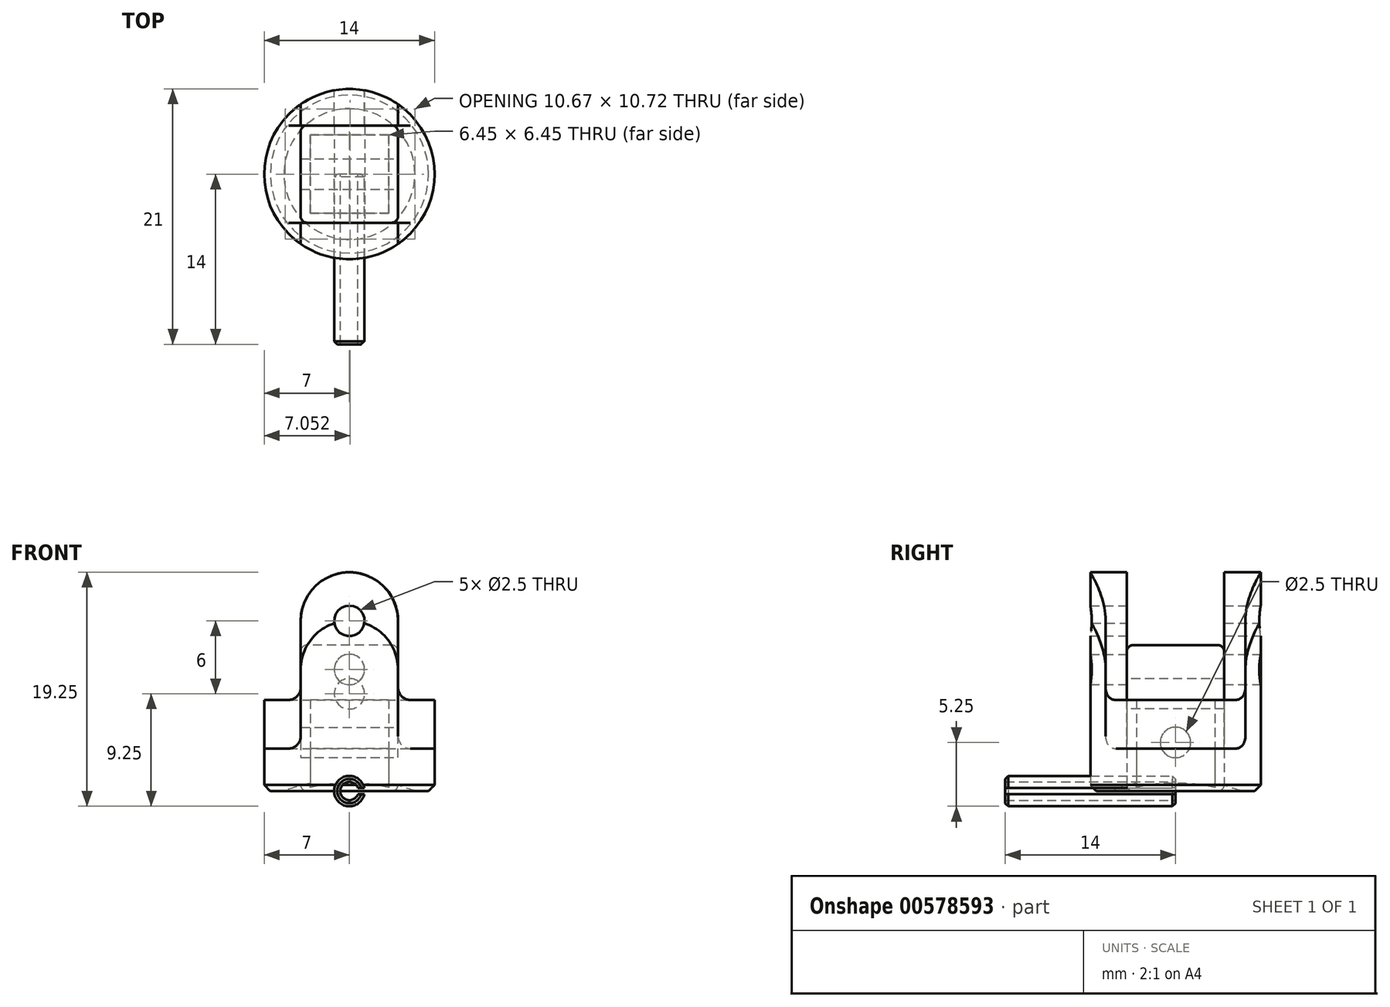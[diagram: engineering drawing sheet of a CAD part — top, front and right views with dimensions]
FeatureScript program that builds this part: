
annotation { "Feature Type Name" : "Feature", "Feature Type Description" : "" }
export const myFeature = defineFeature(function(context is Context, id is Id, definition is map)
    precondition{}
    {
        {
            var Q0;
            Q0=qCreatedBy(makeId("Top.planeOp"),FACE);
            var sketch = newSketch(context, id + "F0", { "sketchPlane" : qUnion([Q0])});
            skLineSegment(sketch, "E0.bottom", {"start": v(3.17, -3.17) * mm, "end": v(-3.17, -3.18) * mm});
            skLineSegment(sketch, "E0.top", {"start": v(3.17, 3.18) * mm, "end": v(-3.17, 3.17) * mm});
            skLineSegment(sketch, "E0.left", {"start": v(3.17, -3.17) * mm, "end": v(3.17, 3.17) * mm});
            skLineSegment(sketch, "E0.right", {"start": v(-3.17, -3.18) * mm, "end": v(-3.17, 3.17) * mm});
            skPoint(sketch, "E0.middle", {"position": v(0, 0) * mm});
            skCircle(sketch, "E1", {"center": v(0, 0) * mm, "radius": 7 * mm});
            skSolve(sketch);
        }
        {
            var Q0;
            Q0=qCreatedBy(makeId("Front.planeOp"),FACE);
            var sketch = newSketch(context, id + "F1", { "sketchPlane" : qUnion([Q0])});
            skLineSegment(sketch, "E2", {"start": v(-7, 0) * mm, "end": v(-7, 3.5) * mm});
            skLineSegment(sketch, "E3", {"start": v(-7, 3.5) * mm, "end": v(-5, 3.5) * mm});
            skLineSegment(sketch, "E4", {"start": v(-4, 4.5) * mm, "end": v(-4, 10) * mm});
            skLineSegment(sketch, "E5", {"start": v(0, 14) * mm, "end": v(0, 14) * mm});
            skLineSegment(sketch, "E6", {"start": v(4, 10) * mm, "end": v(4, 4.5) * mm});
            skLineSegment(sketch, "E7", {"start": v(5, 3.5) * mm, "end": v(7, 3.5) * mm});
            skLineSegment(sketch, "E8", {"start": v(7, 3.5) * mm, "end": v(7, 0) * mm});
            skLineSegment(sketch, "E9", {"start": v(7, 0) * mm, "end": v(-7, 0) * mm});
            skCircle(sketch, "E10", {"center": v(0, 10) * mm, "radius": 1.25 * mm});
            skPoint(sketch, "E11.visualSharp", {"position": v(-4, 3.5) * mm});
            skArc(sketch, "E11.filletArc", {"start": v(-5, 3.5) * mm, "mid": v(-4.3, 3.8) * mm, "end": v(-4, 4.5) * mm});
            skPoint(sketch, "E12.visualSharp", {"position": v(4, 3.5) * mm});
            skArc(sketch, "E12.filletArc", {"start": v(4, 4.5) * mm, "mid": v(4.3, 3.8) * mm, "end": v(5, 3.5) * mm});
            skPoint(sketch, "E13.visualSharp", {"position": v(-4, 14) * mm});
            skArc(sketch, "E13.filletArc", {"start": v(0, 14) * mm, "mid": v(-2.83, 12.83) * mm, "end": v(-4, 10) * mm});
            skPoint(sketch, "E14.visualSharp", {"position": v(4, 14) * mm});
            skArc(sketch, "E14.filletArc", {"start": v(4, 10) * mm, "mid": v(2.83, 12.83) * mm, "end": v(0, 14) * mm});
            skSolve(sketch);
        }
        {
            var Q0;
            Q0=qCreatedBy(makeId("Right.planeOp"),FACE);
            var sketch = newSketch(context, id + "F2", { "sketchPlane" : qUnion([Q0])});
            skLineSegment(sketch, "E15.bottom", {"start": v(4, 3.5) * mm, "end": v(-4, 3.5) * mm});
            skLineSegment(sketch, "E15.top", {"start": v(4, 14) * mm, "end": v(-4, 14) * mm});
            skLineSegment(sketch, "E15.left", {"start": v(4, 3.5) * mm, "end": v(4, 14) * mm});
            skLineSegment(sketch, "E15.right", {"start": v(-4, 3.5) * mm, "end": v(-4, 14) * mm});
            skPoint(sketch, "E15.middle", {"position": v(0, 8.75) * mm});
            skSolve(sketch);
        }
        {
            var Q0;
            Q0=makeQuery(id+"F0.imprint","IMPRINT",FACE,{"disambiguationData":[TD([[makeQuery(id+"F0.imprint","IMPRINT",EDGE,{"derivedFrom":sQuery(id+"F0.wireOp",EDGE,"E0.bottom")}),1.0]])]});
            var Q1;
            Q1=makeQuery(id+"F0.imprint","IMPRINT",FACE,{"disambiguationData":[TD([[makeQuery(id+"F0.imprint","IMPRINT",EDGE,{"derivedFrom":sQuery(id+"F0.wireOp",EDGE,"E0.bottom")}),-1.0]])]});
            extrude(context, id + "F3", {"entities" : qUnion([Q0, Q1]), "depth" : 14 * mm, "offsetDistance" : 25 * mm});
        }
        {
            var Q0;
            Q0 = qSketchRegion(id + "F1", true);
            extrude(context, id + "F4", {"entities" : qUnion([Q0]), "operationType" : NewBodyOperationType.INTERSECT, "endBound" : BoundingType.THROUGH_ALL, "depth" : 25 * mm, "offsetDistance" : 25 * mm, "hasSecondDirection" : true, "secondDirectionBound" : SecondDirectionBoundingType.THROUGH_ALL, "secondDirectionOppositeDirection" : true, "secondDirectionDepth" : 25 * mm});
        }
        {
            var Q0;
            Q0 = qSketchRegion(id + "F2", true);
            extrude(context, id + "F5", {"entities" : qUnion([Q0]), "operationType" : NewBodyOperationType.REMOVE, "endBound" : BoundingType.THROUGH_ALL, "oppositeDirection" : true, "depth" : 25 * mm, "offsetDistance" : 25 * mm, "hasSecondDirection" : true, "secondDirectionBound" : SecondDirectionBoundingType.THROUGH_ALL, "secondDirectionOppositeDirection" : false, "secondDirectionDepth" : 25 * mm});
        }
        {
            var Q0;
            Q0=makeQuery(id+"F3.opExtrude","SWEPT_BODY",BODY,{"disambiguationData":[OSD([sQuery(id+"F0.wireOp",EDGE,"E1")])]});
            transform(context, id + "F6", {"entities" : qUnion([Q0]), "transformType" : TransformType.TRANSLATION_3D, "dx" : 0 * mm, "dy" : 0 * mm, "dz" : 0 * mm, "makeCopy" : true});
        }
        {
            var Q0;
            Q0=makeQuery(id+"F6.opPattern","COPY",BODY,{"derivedFrom":makeQuery(id+"F3.opExtrude","SWEPT_BODY",BODY,{"disambiguationData":[OSD([sQuery(id+"F0.wireOp",EDGE,"E1")])]}),"instanceName":"1"});
            deleteBodies(context, id + "F7", {"entities" : qUnion([Q0])});
        }
        {
            var Q0;
            Q0=makeQuery(id+"F0.imprint","IMPRINT",FACE,{"disambiguationData":[TD([[makeQuery(id+"F0.imprint","IMPRINT",EDGE,{"derivedFrom":sQuery(id+"F0.wireOp",EDGE,"E0.bottom")}),-1.0]])]});
            extrude(context, id + "F8", {"entities" : qUnion([Q0]), "operationType" : NewBodyOperationType.ADD, "oppositeDirection" : true, "depth" : 8.5 * mm, "offsetDistance" : 25 * mm});
        }
        {
            var Q0;
            Q0=makeQuery(id+"F8.opExtrude","CAP_FACE",FACE,{"disambiguationData":[OSD([sQuery(id+"F0.wireOp",EDGE,"E0.bottom"),sQuery(id+"F0.wireOp",EDGE,"E0.top"),sQuery(id+"F0.wireOp",EDGE,"E0.left"),sQuery(id+"F0.wireOp",EDGE,"E0.right")])],"isStart":false});
            var Q1;
            Q1=makeQuery(id+"F8.opExtrude","SWEPT_EDGE",EDGE,{"disambiguationData":[OSD([sQuery(id+"F0.wireOp",EDGE,"E0.bottom"),sQuery(id+"F0.wireOp",EDGE,"E0.right")])]});
            var Q2;
            Q2=makeQuery(id+"F8.opExtrude","SWEPT_EDGE",EDGE,{"disambiguationData":[OSD([sQuery(id+"F0.wireOp",EDGE,"E0.bottom"),sQuery(id+"F0.wireOp",EDGE,"E0.left")])]});
            var Q3;
            Q3=makeQuery(id+"F8.opExtrude","SWEPT_EDGE",EDGE,{"disambiguationData":[OSD([sQuery(id+"F0.wireOp",EDGE,"E0.top"),sQuery(id+"F0.wireOp",EDGE,"E0.right")])]});
            var Q4;
            Q4=makeQuery(id+"F8.opExtrude","SWEPT_EDGE",EDGE,{"disambiguationData":[OSD([sQuery(id+"F0.wireOp",EDGE,"E0.top"),sQuery(id+"F0.wireOp",EDGE,"E0.left")])]});
            var Q5;
            Q5=makeQuery(id+"F3.opExtrude","CAP_EDGE",EDGE,{"disambiguationData":[OSD([sQuery(id+"F0.wireOp",EDGE,"E1")])],"isStart":true});
            chamfer(context, id + "F9", {"entities" : qUnion([Q0, Q1, Q2, Q3, Q4, Q5]), "width" : 0.5 * mm, "tangentPropagation" : true});
        }
        {
            var Q0;
            Q0=makeQuery(id+"F8.opExtrude","SWEPT_FACE",FACE,{"disambiguationData":[OSD([sQuery(id+"F0.wireOp",EDGE,"E0.bottom")])]});
            var sketch = newSketch(context, id + "F10", { "sketchPlane" : qUnion([Q0])});
            skPoint(sketch, "E16", {"position": v(0, -5) * mm});
            skSolve(sketch);
        }
        {
            var Q0;
            Q0=sQuery(id+"F10.wireOp",VERTEX,"E16");
            var Q1;
            Q1=makeQuery(id+"F3.opExtrude","SWEPT_BODY",BODY,{"disambiguationData":[OSD([sQuery(id+"F0.wireOp",EDGE,"E1")])]});
            hole(context, id + "F11", {"style" : HoleStyle.SIMPLE, "endStyle" : HoleEndStyle.BLIND, "holeDiameter" : 2.5 * mm, "holeDepth" : 4 * mm, "tappedDepth" : 20 * mm, "tapClearance" : 0, "startFromSketch" : true, "locations" : qUnion([Q0]), "scope" : qUnion([Q1])});
        }
        {
            var Q0;
            Q0=qCreatedBy(makeId("Front.planeOp"),FACE);
            var sketch = newSketch(context, id + "F12", { "sketchPlane" : qUnion([Q0])});
            skLineSegment(sketch, "E17", {"start": v(-7, 0) * mm, "end": v(-7, 7.5) * mm});
            skLineSegment(sketch, "E18", {"start": v(-7, 7.5) * mm, "end": v(-5, 7.5) * mm});
            skLineSegment(sketch, "E19", {"start": v(-4, 8.5) * mm, "end": v(-4, 14) * mm});
            skLineSegment(sketch, "E20", {"start": v(0, 18) * mm, "end": v(0, 18) * mm});
            skLineSegment(sketch, "E21", {"start": v(4, 14) * mm, "end": v(4, 8.5) * mm});
            skLineSegment(sketch, "E22", {"start": v(5, 7.5) * mm, "end": v(7, 7.5) * mm});
            skLineSegment(sketch, "E23", {"start": v(7, 7.5) * mm, "end": v(7, 0) * mm});
            skLineSegment(sketch, "E24", {"start": v(7, 0) * mm, "end": v(-7, 0) * mm});
            skPoint(sketch, "E25.visualSharp", {"position": v(-4, 7.5) * mm});
            skArc(sketch, "E25.filletArc", {"start": v(-5, 7.5) * mm, "mid": v(-4.3, 7.8) * mm, "end": v(-4, 8.5) * mm});
            skPoint(sketch, "E26.visualSharp", {"position": v(4, 7.5) * mm});
            skArc(sketch, "E26.filletArc", {"start": v(4, 8.5) * mm, "mid": v(4.3, 7.8) * mm, "end": v(5, 7.5) * mm});
            skPoint(sketch, "E27.visualSharp", {"position": v(-4, 18) * mm});
            skArc(sketch, "E27.filletArc", {"start": v(0, 18) * mm, "mid": v(-2.83, 16.83) * mm, "end": v(-4, 14) * mm});
            skPoint(sketch, "E28.visualSharp", {"position": v(4, 18) * mm});
            skArc(sketch, "E28.filletArc", {"start": v(4, 14) * mm, "mid": v(2.83, 16.83) * mm, "end": v(0, 18) * mm});
            skCircle(sketch, "E29", {"center": v(0, 14) * mm, "radius": 1.25 * mm});
            skSolve(sketch);
        }
        {
            var Q0;
            Q0=makeQuery(id+"F0.imprint","IMPRINT",FACE,{"disambiguationData":[TD([[makeQuery(id+"F0.imprint","IMPRINT",EDGE,{"derivedFrom":sQuery(id+"F0.wireOp",EDGE,"E0.bottom")}),1.0]])]});
            var Q1;
            Q1=makeQuery(id+"F0.imprint","IMPRINT",FACE,{"disambiguationData":[TD([[makeQuery(id+"F0.imprint","IMPRINT",EDGE,{"derivedFrom":sQuery(id+"F0.wireOp",EDGE,"E0.bottom")}),-1.0]])]});
            extrude(context, id + "F13", {"entities" : qUnion([Q0, Q1]), "depth" : 18 * mm, "offsetDistance" : 25 * mm});
        }
        {
            var Q0;
            Q0 = qSketchRegion(id + "F12", true);
            extrude(context, id + "F14", {"entities" : qUnion([Q0]), "operationType" : NewBodyOperationType.INTERSECT, "endBound" : BoundingType.THROUGH_ALL, "depth" : 25 * mm, "offsetDistance" : 25 * mm, "hasSecondDirection" : true, "secondDirectionBound" : SecondDirectionBoundingType.THROUGH_ALL, "secondDirectionOppositeDirection" : true, "secondDirectionDepth" : 25 * mm});
        }
        {
            var Q0;
            Q0=qCreatedBy(makeId("Right.planeOp"),FACE);
            var sketch = newSketch(context, id + "F15", { "sketchPlane" : qUnion([Q0])});
            skLineSegment(sketch, "E30.bottom", {"start": v(4, 7.5) * mm, "end": v(-4, 7.5) * mm});
            skLineSegment(sketch, "E30.top", {"start": v(4, 18) * mm, "end": v(-4, 18) * mm});
            skLineSegment(sketch, "E30.left", {"start": v(4, 7.5) * mm, "end": v(4, 18) * mm});
            skLineSegment(sketch, "E30.right", {"start": v(-4, 7.5) * mm, "end": v(-4, 18) * mm});
            skPoint(sketch, "E30.middle", {"position": v(0, 12.75) * mm});
            skSolve(sketch);
        }
        {
            var Q0;
            Q0 = qSketchRegion(id + "F15", true);
            extrude(context, id + "F16", {"entities" : qUnion([Q0]), "operationType" : NewBodyOperationType.REMOVE, "endBound" : BoundingType.THROUGH_ALL, "oppositeDirection" : true, "depth" : 25 * mm, "offsetDistance" : 25 * mm, "hasSecondDirection" : true, "secondDirectionBound" : SecondDirectionBoundingType.THROUGH_ALL, "secondDirectionOppositeDirection" : false, "secondDirectionDepth" : 25 * mm});
        }
        {
            var Q0;
            Q0=makeQuery(id+"F0.imprint","IMPRINT",FACE,{"disambiguationData":[TD([[makeQuery(id+"F0.imprint","IMPRINT",EDGE,{"derivedFrom":sQuery(id+"F0.wireOp",EDGE,"E0.bottom")}),1.0]])]});
            var sketch = newSketch(context, id + "F17", { "sketchPlane" : qUnion([Q0])});
            skLineSegment(sketch, "E31.0", {"start": v(3.23, -3.23) * mm, "end": v(3.23, 3.23) * mm});
            skLineSegment(sketch, "E31.1", {"start": v(-3.23, -3.23) * mm, "end": v(3.22, -3.23) * mm});
            skLineSegment(sketch, "E31.2", {"start": v(-3.23, 3.23) * mm, "end": v(-3.23, -3.23) * mm});
            skLineSegment(sketch, "E31.3", {"start": v(3.23, 3.23) * mm, "end": v(-3.22, 3.23) * mm});
            skSolve(sketch);
        }
        {
            var Q0;
            Q0 = qSketchRegion(id + "F17", true);
            extrude(context, id + "F18", {"entities" : qUnion([Q0]), "operationType" : NewBodyOperationType.REMOVE, "endBound" : BoundingType.THROUGH_ALL, "depth" : 25 * mm, "offsetDistance" : 25 * mm});
        }
        {
            var Q0;
            Q0=makeQuery(id+"F13.opExtrude","CAP_EDGE",EDGE,{"disambiguationData":[OSD([sQuery(id+"F0.wireOp",EDGE,"E1")])],"isStart":true});
            chamfer(context, id + "F19", {"entities" : qUnion([Q0]), "width" : 0.5 * mm, "tangentPropagation" : true});
        }
        {
            var Q0;
            Q0=sQuery(id+"F0.wireOp",VERTEX,"E0.right.start");
            var Q1;
            Q1=sQuery(id+"F0.wireOp",VERTEX,"E0.left.end");
            var Q2;
            Q2=sQuery(id+"F12.wireOp",VERTEX,"E29.center");
            cPlane(context, id + "F20", {"entities" : qUnion([Q0, Q1, Q2]), "cplaneType" : CPlaneType.THREE_POINT, "offset" : 25 * mm, "width" : 150 * mm, "height" : 150 * mm});
        }
        {
            var Q0;
            Q0=qCreatedBy(id+"F20.planeOp",FACE);
            var sketch = newSketch(context, id + "F21", { "sketchPlane" : qUnion([Q0])});
            skLineSegment(sketch, "E32", {"start": v(0, -29) * mm, "end": v(0, 1) * mm});
            skArc(sketch, "E33", {"start": v(0, 1) * mm, "mid": v(-15, -14.06) * mm, "end": v(0.12, -29) * mm});
            skSolve(sketch);
        }
        {
            var Q0;
            {var subQ0=sQuery(id+"F21.wireOp",EDGE,"E32");Q0=makeQuery(id+"F21.imprint","IMPRINT",FACE,{"disambiguationData":[TD([[makeQuery(id+"F21.imprint","IMPRINT",EDGE,{"derivedFrom":subQ0}),1.0]])]});}
            var Q1;
            Q1=sQuery(id+"F21.wireOp",EDGE,"E32");
            revolve(context, id + "F22", {"operationType" : NewBodyOperationType.REMOVE, "entities" : qUnion([Q0]), "axis" : qUnion([Q1]), "revolveType" : RevolveType.FULL, "oppositeDirection" : true});
        }
        {
            var Q0;
            Q0=qCreatedBy(makeId("Top.planeOp"),FACE);
            var sketch = newSketch(context, id + "F23", { "sketchPlane" : qUnion([Q0])});
            skLineSegment(sketch, "E34.bottom", {"start": v(3.5, -4) * mm, "end": v(-3.5, -4) * mm});
            skLineSegment(sketch, "E34.top", {"start": v(3.5, 4) * mm, "end": v(-3.5, 4) * mm});
            skLineSegment(sketch, "E34.left", {"start": v(4, -3.5) * mm, "end": v(4, 3.5) * mm});
            skLineSegment(sketch, "E34.right", {"start": v(-4, -3.5) * mm, "end": v(-4, 3.5) * mm});
            skPoint(sketch, "E34.middle", {"position": v(0, 0) * mm});
            skPoint(sketch, "E35.visualSharp", {"position": v(-4, 4) * mm});
            skArc(sketch, "E35.filletArc", {"start": v(-3.5, 4) * mm, "mid": v(-3.85, 3.85) * mm, "end": v(-4, 3.5) * mm});
            skPoint(sketch, "E36.visualSharp", {"position": v(4, 4) * mm});
            skArc(sketch, "E36.filletArc", {"start": v(4, 3.5) * mm, "mid": v(3.85, 3.85) * mm, "end": v(3.5, 4) * mm});
            skPoint(sketch, "E37.visualSharp", {"position": v(-4, -4) * mm});
            skArc(sketch, "E37.filletArc", {"start": v(-4, -3.5) * mm, "mid": v(-3.85, -3.85) * mm, "end": v(-3.5, -4) * mm});
            skPoint(sketch, "E38.visualSharp", {"position": v(4, -4) * mm});
            skArc(sketch, "E38.filletArc", {"start": v(3.5, -4) * mm, "mid": v(3.85, -3.85) * mm, "end": v(4, -3.5) * mm});
            skSolve(sketch);
        }
        {
            var Q0;
            Q0 = qSketchRegion(id + "F23", true);
            extrude(context, id + "F24", {"entities" : qUnion([Q0]), "depth" : 12 * mm, "offsetDistance" : 25 * mm});
        }
        {
            var Q0;
            Q0=makeQuery(id+"F24.opExtrude","CAP_EDGE",EDGE,{"disambiguationData":[OSD([sQuery(id+"F23.wireOp",EDGE,"E34.bottom")])],"isStart":false});
            var Q1;
            Q1=makeQuery(id+"F24.opExtrude","CAP_EDGE",EDGE,{"disambiguationData":[OSD([sQuery(id+"F23.wireOp",EDGE,"E34.bottom")])],"isStart":true});
            fillet(context, id + "F25", {"entities" : qUnion([Q0, Q1]), "radius" : 0.5 * mm, "tangentPropagation" : true, "allowEdgeOverflow" : false});
        }
        {
            var Q0;
            Q0=makeQuery(id+"F24.opExtrude","SWEPT_FACE",FACE,{"disambiguationData":[OSD([sQuery(id+"F23.wireOp",EDGE,"E34.bottom")])]});
            var sketch = newSketch(context, id + "F26", { "sketchPlane" : qUnion([Q0])});
            skPoint(sketch, "E39", {"position": v(0, 8) * mm});
            skSolve(sketch);
        }
        {
            var Q0;
            Q0=makeQuery(id+"F24.opExtrude","SWEPT_FACE",FACE,{"disambiguationData":[OSD([sQuery(id+"F23.wireOp",EDGE,"E34.left")])]});
            var sketch = newSketch(context, id + "F27", { "sketchPlane" : qUnion([Q0])});
            skPoint(sketch, "E40", {"position": v(0, 4) * mm});
            skSolve(sketch);
        }
        {
            var Q0;
            Q0=sQuery(id+"F27.wireOp",VERTEX,"E40");
            var Q1;
            Q1=makeQuery(id+"F24.opExtrude","SWEPT_BODY",BODY,{"disambiguationData":[OSD([sQuery(id+"F23.wireOp",EDGE,"E34.bottom"),sQuery(id+"F23.wireOp",EDGE,"E34.top"),sQuery(id+"F23.wireOp",EDGE,"E34.left"),sQuery(id+"F23.wireOp",EDGE,"E34.right"),sQuery(id+"F23.wireOp",EDGE,"E35.filletArc"),sQuery(id+"F23.wireOp",EDGE,"E36.filletArc"),sQuery(id+"F23.wireOp",EDGE,"E37.filletArc"),sQuery(id+"F23.wireOp",EDGE,"E38.filletArc")])]});
            hole(context, id + "F28", {"style" : HoleStyle.SIMPLE, "endStyle" : HoleEndStyle.THROUGH, "holeDiameter" : 2.5 * mm, "tappedDepth" : 20 * mm, "tapClearance" : 0, "startFromSketch" : true, "locations" : qUnion([Q0]), "scope" : qUnion([Q1])});
        }
        {
            var Q0;
            Q0=sQuery(id+"F26.wireOp",VERTEX,"E39");
            var Q1;
            Q1=makeQuery(id+"F24.opExtrude","SWEPT_BODY",BODY,{"disambiguationData":[OSD([sQuery(id+"F23.wireOp",EDGE,"E34.bottom"),sQuery(id+"F23.wireOp",EDGE,"E34.top"),sQuery(id+"F23.wireOp",EDGE,"E34.left"),sQuery(id+"F23.wireOp",EDGE,"E34.right"),sQuery(id+"F23.wireOp",EDGE,"E35.filletArc"),sQuery(id+"F23.wireOp",EDGE,"E36.filletArc"),sQuery(id+"F23.wireOp",EDGE,"E37.filletArc"),sQuery(id+"F23.wireOp",EDGE,"E38.filletArc")])]});
            hole(context, id + "F29", {"style" : HoleStyle.SIMPLE, "endStyle" : HoleEndStyle.THROUGH, "holeDiameter" : 2.5 * mm, "tappedDepth" : 20 * mm, "tapClearance" : 0, "startFromSketch" : true, "locations" : qUnion([Q0]), "scope" : qUnion([Q1])});
        }
        {
            var Q0;
            Q0=qCreatedBy(makeId("Front.planeOp"),FACE);
            var sketch = newSketch(context, id + "F30", { "sketchPlane" : qUnion([Q0])});
            skArc(sketch, "E41", {"start": v(1.22, 0.25) * mm, "mid": v(-1.25, 0) * mm, "end": v(1.22, -0.25) * mm});
            skArc(sketch, "E42", {"start": v(0.7, 0.25) * mm, "mid": v(-0.75, 0) * mm, "end": v(0.7, -0.25) * mm});
            skLineSegment(sketch, "E43", {"start": v(0.7, 0.25) * mm, "end": v(1.22, 0.25) * mm});
            skLineSegment(sketch, "E44", {"start": v(0.7, -0.25) * mm, "end": v(1.22, -0.25) * mm});
            skSolve(sketch);
        }
        {
            var Q0;
            Q0=makeQuery(id+"F30.imprint","IMPRINT",FACE,{"disambiguationData":[TD([[makeQuery(id+"F30.imprint","IMPRINT",EDGE,{"derivedFrom":sQuery(id+"F30.wireOp",EDGE,"E41")}),1.0]])]});
            extrude(context, id + "F31", {"entities" : qUnion([Q0]), "depth" : 14 * mm, "offsetDistance" : 25 * mm});
        }
        {
            var Q0;
            Q0=makeQuery(id+"F31.opExtrude","CAP_EDGE",EDGE,{"disambiguationData":[OSD([sQuery(id+"F30.wireOp",EDGE,"E41")])],"isStart":false});
            var Q1;
            Q1=makeQuery(id+"F31.opExtrude","CAP_EDGE",EDGE,{"disambiguationData":[OSD([sQuery(id+"F30.wireOp",EDGE,"E41")])],"isStart":true});
            chamfer(context, id + "F32", {"entities" : qUnion([Q0, Q1]), "width" : 0.25 * mm, "tangentPropagation" : true});
        }
        {
            var Q0;
            Q0=sQuery(id+"F1.wireOp",EDGE,"E10");
            var Q1;
            Q1=makeQuery(id+"F5.boolean.opBoolean","COPY",FACE,{"derivedFrom":makeQuery(id+"F5.opExtrude","SWEPT_FACE",FACE,{"disambiguationData":[OSD([sQuery(id+"F2.wireOp",EDGE,"E15.right")])]})});
            var Q2;
            Q2=makeQuery(id+"F5.boolean.opBoolean","COPY",FACE,{"derivedFrom":makeQuery(id+"F5.opExtrude","SWEPT_FACE",FACE,{"disambiguationData":[OSD([sQuery(id+"F2.wireOp",EDGE,"E15.left")])]})});
            extrude(context, id + "F33", {"bodyType" : ToolBodyType.SURFACE, "surfaceEntities" : qUnion([Q0]), "endBound" : BoundingType.UP_TO_SURFACE, "depth" : 25 * mm, "endBoundEntityFace" : qUnion([Q1]), "offsetDistance" : 25 * mm, "hasSecondDirection" : true, "secondDirectionBound" : SecondDirectionBoundingType.UP_TO_SURFACE, "secondDirectionOppositeDirection" : true, "secondDirectionDepth" : 25 * mm, "secondDirectionBoundEntityFace" : qUnion([Q2])});
        }
        {
            var Q0;
            Q0=sQuery(id+"F12.wireOp",EDGE,"E29");
            var Q1;
            Q1=makeQuery(id+"F16.boolean.opBoolean","COPY",FACE,{"derivedFrom":makeQuery(id+"F16.opExtrude","SWEPT_FACE",FACE,{"disambiguationData":[OSD([sQuery(id+"F15.wireOp",EDGE,"E30.right")])]})});
            var Q2;
            Q2=makeQuery(id+"F16.boolean.opBoolean","COPY",FACE,{"derivedFrom":makeQuery(id+"F16.opExtrude","SWEPT_FACE",FACE,{"disambiguationData":[OSD([sQuery(id+"F15.wireOp",EDGE,"E30.left")])]})});
            extrude(context, id + "F34", {"bodyType" : ToolBodyType.SURFACE, "surfaceEntities" : qUnion([Q0]), "endBound" : BoundingType.UP_TO_SURFACE, "depth" : 25 * mm, "endBoundEntityFace" : qUnion([Q1]), "offsetDistance" : 25 * mm, "hasSecondDirection" : true, "secondDirectionBound" : SecondDirectionBoundingType.UP_TO_SURFACE, "secondDirectionOppositeDirection" : true, "secondDirectionDepth" : 25 * mm, "secondDirectionBoundEntityFace" : qUnion([Q2])});
        }
    });
